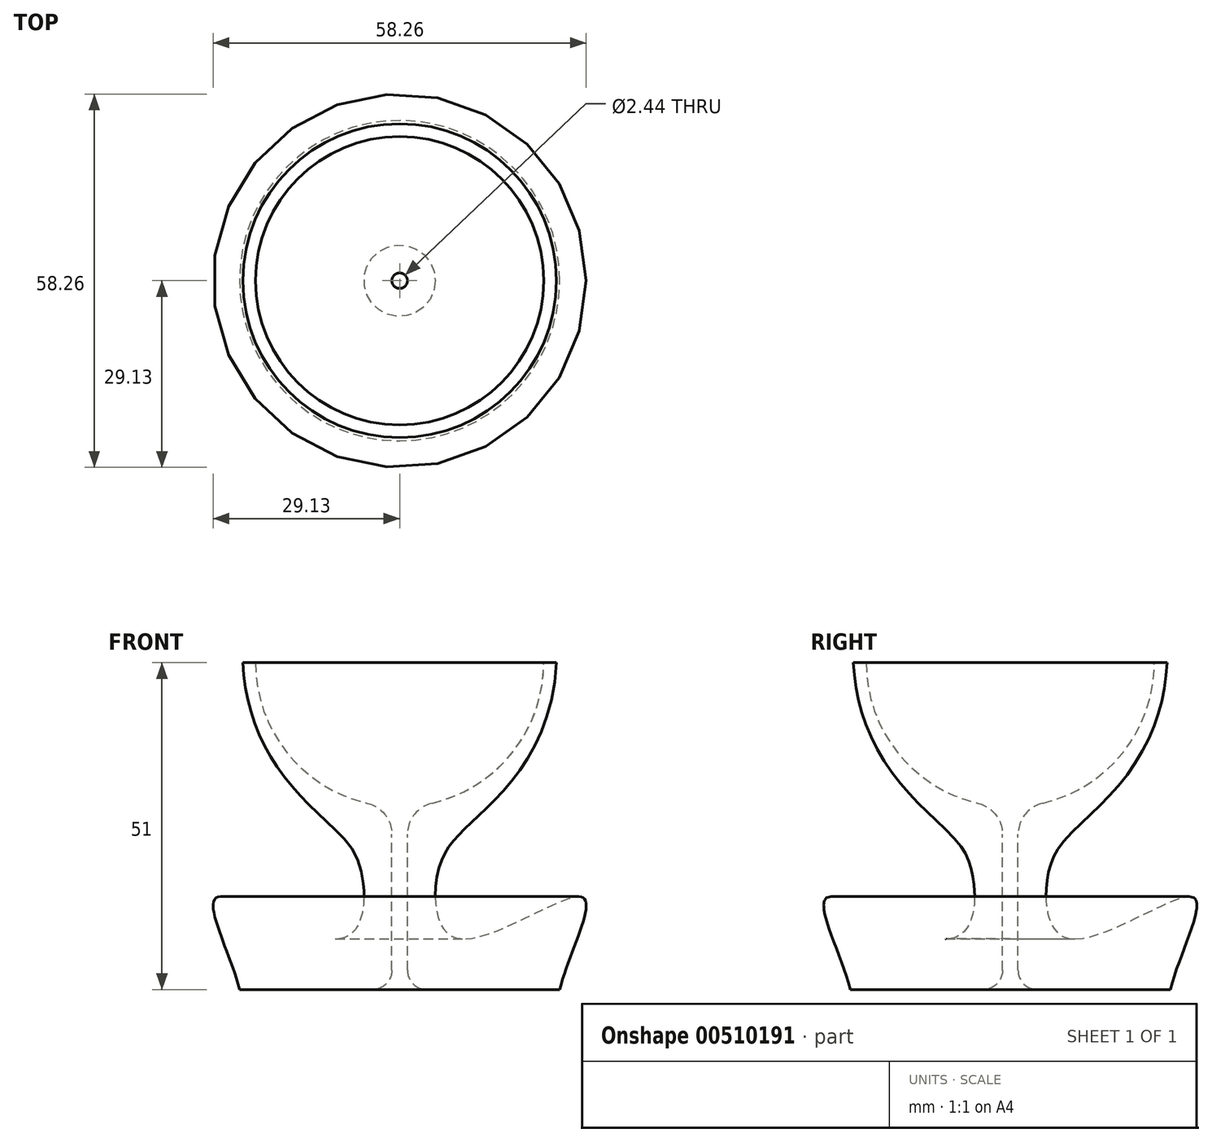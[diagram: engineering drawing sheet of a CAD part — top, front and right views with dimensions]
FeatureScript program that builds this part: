
annotation { "Feature Type Name" : "Feature", "Feature Type Description" : "" }
export const myFeature = defineFeature(function(context is Context, id is Id, definition is map)
    precondition{}
    {
        {
            var Q0;
            Q0=qCreatedBy(makeId("Front.planeOp"),FACE);
            var sketch = newSketch(context, id + "F0", { "sketchPlane" : qUnion([Q0])});
            skCircle(sketch, "E0", {"center": v(0, 0) * mm, "radius": 22.5 * mm});
            skLineSegment(sketch, "E1", {"start": v(0, 0) * mm, "end": v(0, -51) * mm});
            skLineSegment(sketch, "E2", {"start": v(0, -51) * mm, "end": v(-25, -51) * mm});
            skLineSegment(sketch, "E3", {"start": v(0, 0) * mm, "end": v(-24.5, 0) * mm});
            skFitSpline(sketch, "E4", {"points": [v(-24.5, 0) * mm, v(-11.07, -25.07) * mm, v(-5.93, -32.88) * mm, v(-9.14, -43.03) * mm, v(-28.52, -36.6) * mm, v(-25, -51) * mm], "startDerivative": vector(8.56, -154.25) * mm, "endDerivative": vector(21.18, -86.7) * mm});
            skLineSegment(sketch, "E5", {"start": v(-1.22, -51) * mm, "end": v(-1.22, -22.47) * mm});
            skSolve(sketch);
        }
        {
            var Q0;
            {var subQ0=sQuery(id+"F0.wireOp",EDGE,"E4");Q0=makeQuery(id+"F0.imprint","IMPRINT",FACE,{"disambiguationData":[TD([[makeQuery(id+"F0.imprint","IMPRINT",EDGE,{"derivedFrom":subQ0}),1.0]])]});}
            var Q1;
            Q1=sQuery(id+"F0.wireOp",EDGE,"E1");
            revolve(context, id + "F1", {"entities" : qUnion([Q0]), "axis" : qUnion([Q1]), "revolveType" : RevolveType.FULL});
        }
        {
            var Q0;
            Q0=makeQuery(id+"F1.opRevolve","SWEPT_EDGE",EDGE,{"disambiguationData":[OSD([sQuery(id+"F0.wireOp",EDGE,"E0"),sQuery(id+"F0.wireOp",EDGE,"E5")])]});
            fillet(context, id + "F2", {"entities" : qUnion([Q0]), "radius" : 5 * mm, "tangentPropagation" : true, "allowEdgeOverflow" : false});
        }
        {
            var Q0;
            Q0=makeQuery(id+"F1.opRevolve","SWEPT_EDGE",EDGE,{"disambiguationData":[OSD([sQuery(id+"F0.wireOp",EDGE,"E2"),sQuery(id+"F0.wireOp",EDGE,"E5")])]});
            fillet(context, id + "F3", {"entities" : qUnion([Q0]), "radius" : 3 * mm, "tangentPropagation" : true, "allowEdgeOverflow" : false});
        }
    });
